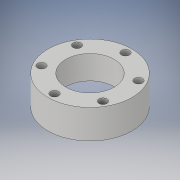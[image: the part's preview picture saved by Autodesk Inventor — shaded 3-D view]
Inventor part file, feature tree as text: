
AUTODESK INVENTOR PART (.ipt)
format: ipt  version: 2019.3 (Build 233278000, 278)  size: 152,576 bytes
history: native  units: mm
features: sketch x2, revolve x1, hole x1
ambient origin geometry x8: Origin, YZ Plane, XZ Plane, XY Plane, X Axis, Y Axis, Z Axis, Center Point
bodies: Body1 (feature_tree)
feature tree (4):
  revolve  "Revolution1"  [1 undecoded]
  hole  "Hole1"  [1 undecoded]
  sketch  "Sketch3"  dims[d5=26.0mm d6=21.75mm]
  sketch  "Sketch4"  dims[d7=0.3mm d8=18.0mm d9=15.0mm d10=3.0mm d11=90.0deg d12=22.0mm d13=60.0mm d15=360.0deg d17=5.0mm d18=6.0mm d19=4.0mm d20=2.0mm d21=90.0deg d22=8.0mm d23=20.594885mm]
note: 2 required parameter values undecoded (feature->parameter linkage not recoverable at this tier; creation-order binding heuristic only, values carry confidence <= 0.55)